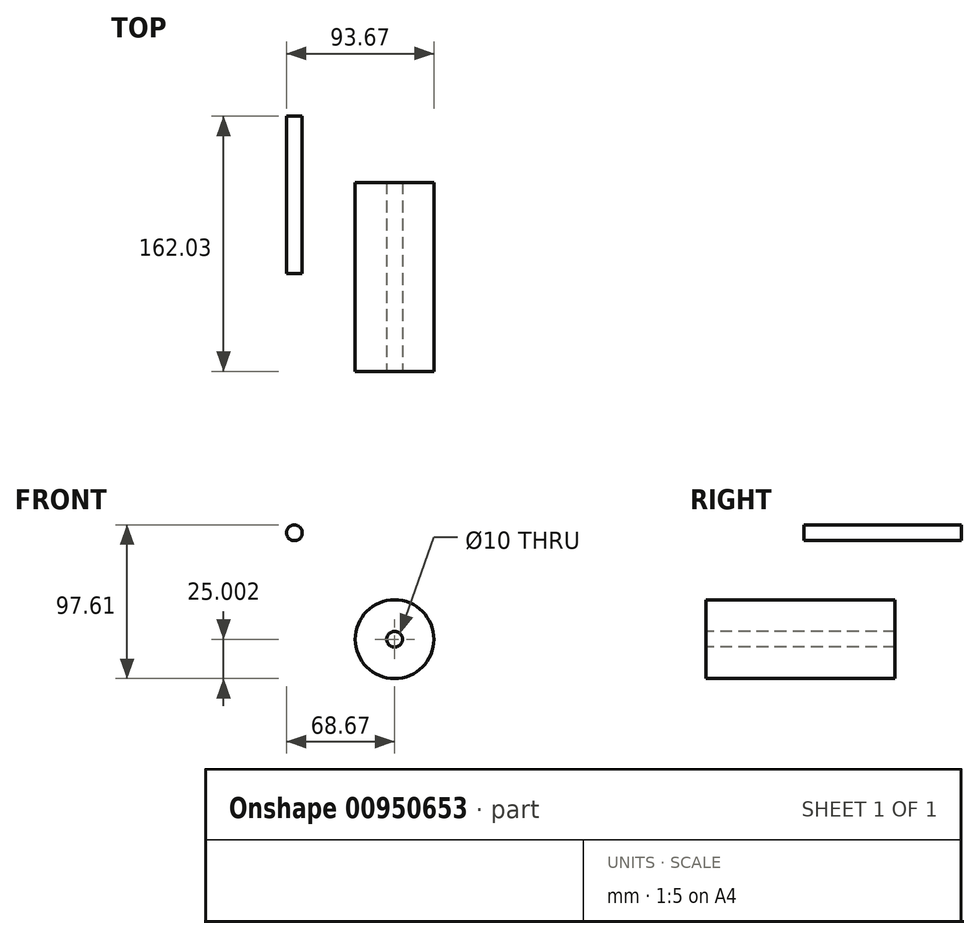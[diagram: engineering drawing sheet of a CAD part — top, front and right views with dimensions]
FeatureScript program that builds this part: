
annotation { "Feature Type Name" : "Feature", "Feature Type Description" : "" }
export const myFeature = defineFeature(function(context is Context, id is Id, definition is map)
    precondition{}
    {
        {
            var Q0;
            Q0=qCreatedBy(makeId("Front.planeOp"),FACE);
            var sketch = newSketch(context, id + "F0", { "sketchPlane" : qUnion([Q0])});
            skCircle(sketch, "E0", {"center": v(-63.67, 28.61) * mm, "radius": 5 * mm});
            skSolve(sketch);
        }
        {
            var Q0;
            Q0 = qSketchRegion(id + "F0", true);
            extrude(context, id + "F1", {"entities" : qUnion([Q0]), "oppositeDirection" : true, "depth" : 100 * mm, "offsetDistance" : 25 * mm});
        }
        {
            var Q0;
            Q0=qCreatedBy(makeId("Right.planeOp"),FACE);
            var sketch = newSketch(context, id + "F2", { "sketchPlane" : qUnion([Q0])});
            skLineSegment(sketch, "E1", {"start": v(-62.03, -14) * mm, "end": v(57.97, -14) * mm});
            skLineSegment(sketch, "E2", {"start": v(-62.03, -14) * mm, "end": v(-62.03, -34) * mm});
            skLineSegment(sketch, "E3", {"start": v(-62.03, -34) * mm, "end": v(57.97, -34) * mm});
            skLineSegment(sketch, "E4", {"start": v(57.97, -34) * mm, "end": v(57.97, -14) * mm});
            skLineSegment(sketch, "E5", {"start": v(-62.03, -34) * mm, "end": v(-62.03, -39) * mm, "construction": true});
            skLineSegment(sketch, "E6", {"start": v(-62.03, -39) * mm, "end": v(57.97, -39) * mm, "construction": true});
            skLineSegment(sketch, "E7", {"start": v(57.97, -39) * mm, "end": v(57.97, -34) * mm, "construction": true});
            skSolve(sketch);
        }
        {
            var Q0;
            Q0=makeQuery(id+"F2.imprint","IMPRINT",FACE,{"disambiguationData":[TD([[makeQuery(id+"F2.imprint","IMPRINT",EDGE,{"derivedFrom":sQuery(id+"F2.wireOp",EDGE,"E1")}),-1.0]])]});
            var Q1;
            Q1=sQuery(id+"F2.wireOp",EDGE,"E6");
            revolve(context, id + "F3", {"surfaceOperationType" : NewSurfaceOperationType.NEW, "entities" : qUnion([Q0]), "axis" : qUnion([Q1]), "revolveType" : RevolveType.FULL});
        }
    });
